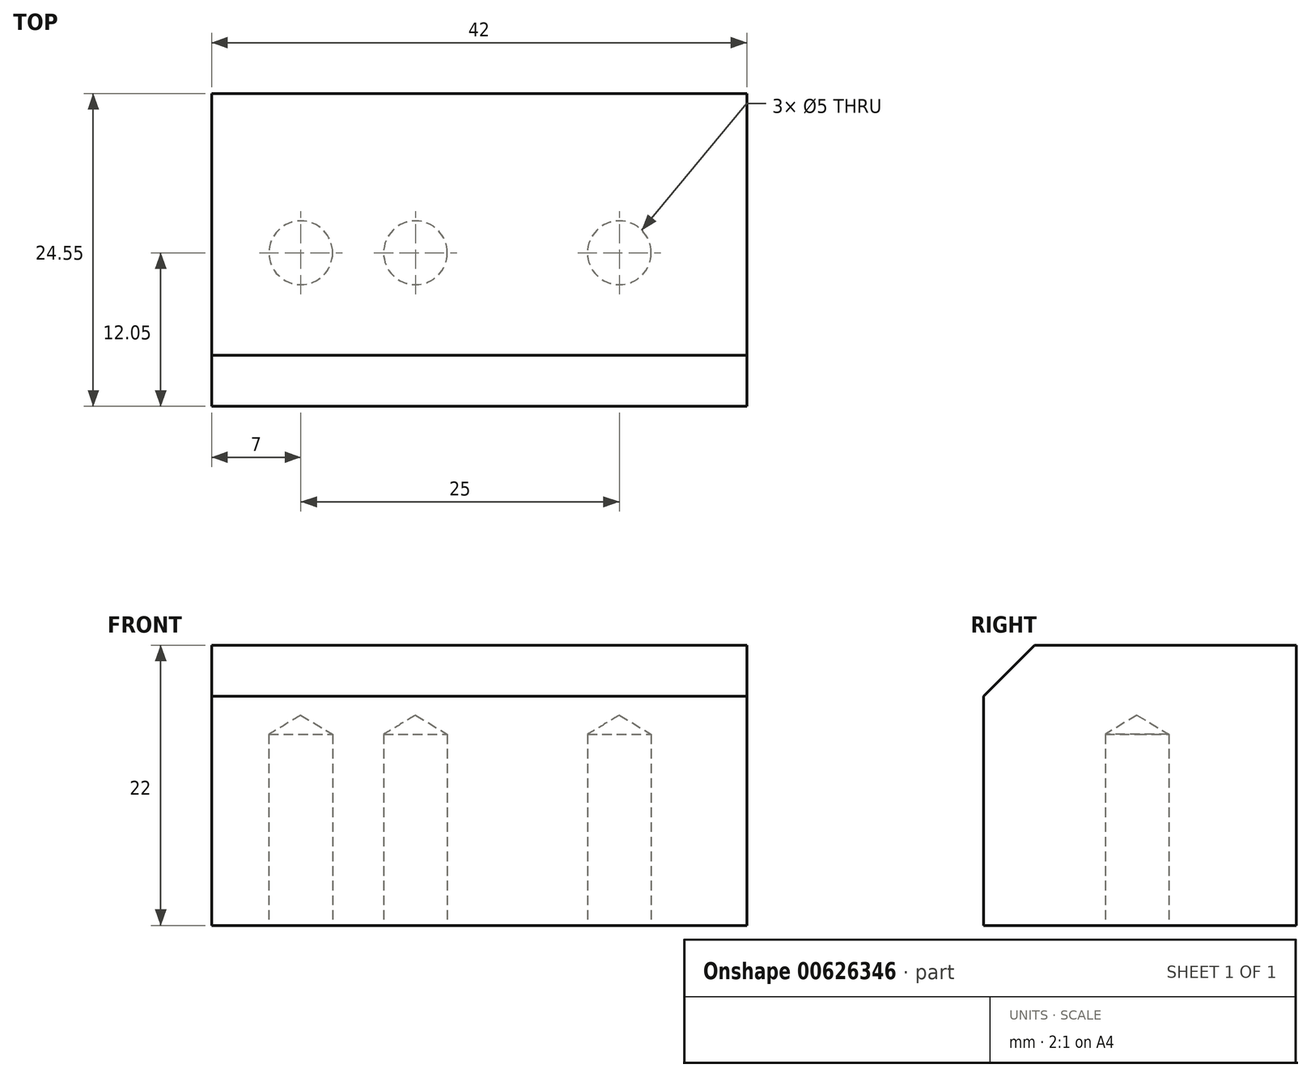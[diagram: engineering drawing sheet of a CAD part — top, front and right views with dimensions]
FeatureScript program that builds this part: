
annotation { "Feature Type Name" : "Feature", "Feature Type Description" : "" }
export const myFeature = defineFeature(function(context is Context, id is Id, definition is map)
    precondition{}
    {
        {
            var Q0;
            Q0=qCreatedBy(makeId("Right.planeOp"),FACE);
            var sketch = newSketch(context, id + "F0", { "sketchPlane" : qUnion([Q0])});
            skLineSegment(sketch, "E0.bottom", {"start": v(0, 0) * mm, "end": v(-24.55, 0) * mm});
            skLineSegment(sketch, "E0.top", {"start": v(0, 22) * mm, "end": v(-24.55, 22) * mm});
            skLineSegment(sketch, "E0.left", {"start": v(0, 0) * mm, "end": v(0, 22) * mm});
            skLineSegment(sketch, "E0.right", {"start": v(-24.55, 0) * mm, "end": v(-24.55, 22) * mm});
            skSolve(sketch);
        }
        {
            var Q0;
            Q0 = qSketchRegion(id + "F0", true);
            extrude(context, id + "F1", {"entities" : qUnion([Q0]), "depth" : 42 * mm, "offsetDistance" : 25 * mm});
        }
        {
            var Q0;
            Q0=makeQuery(id+"F1.opExtrude","SWEPT_EDGE",EDGE,{"disambiguationData":[OSD([sQuery(id+"F0.wireOp",EDGE,"E0.top"),sQuery(id+"F0.wireOp",EDGE,"E0.right")])]});
            chamfer(context, id + "F2", {"entities" : qUnion([Q0]), "width" : 4 * mm, "tangentPropagation" : true});
        }
        {
            var Q0;
            Q0=makeQuery(id+"F1.opExtrude","SWEPT_FACE",FACE,{"disambiguationData":[OSD([sQuery(id+"F0.wireOp",EDGE,"E0.bottom")])]});
            var sketch = newSketch(context, id + "F3", { "sketchPlane" : qUnion([Q0])});
            skPoint(sketch, "E1", {"position": v(32, 12.5) * mm});
            skPoint(sketch, "E2", {"position": v(16, 12.5) * mm});
            skPoint(sketch, "E3", {"position": v(7, 12.5) * mm});
            skSolve(sketch);
        }
        {
            var Q0;
            Q0=sQuery(id+"F3.wireOp",VERTEX,"E1");
            var Q1;
            Q1=sQuery(id+"F3.wireOp",VERTEX,"E2");
            var Q2;
            Q2=sQuery(id+"F3.wireOp",VERTEX,"E3");
            var Q3;
            Q3=makeQuery(id+"F1.opExtrude","SWEPT_BODY",BODY,{"disambiguationData":[OSD([sQuery(id+"F0.wireOp",EDGE,"E0.bottom"),sQuery(id+"F0.wireOp",EDGE,"E0.top"),sQuery(id+"F0.wireOp",EDGE,"E0.left"),sQuery(id+"F0.wireOp",EDGE,"E0.right")])]});
            hole(context, id + "F4", {"style" : HoleStyle.SIMPLE, "endStyle" : HoleEndStyle.BLIND, "standardTappedOrClearance" : lookupTablePath({ "standard" : "ISO", "engagement" : "75%", "pitch" : "1 mm", "size" : "M6", "type" : "Tapped" }), "standardBlindInLast" : lookupTablePath({ "standard" : "ISO", "engagement" : "75%", "pitch" : "1 mm", "size" : "M6", "type" : "Tapped" }), "holeDiameter" : 5 * mm, "majorDiameter" : 6 * mm, "showTappedDepth" : true, "holeDepth" : 15 * mm, "isTappedThrough" : true, "tappedDepth" : 12 * mm, "tapClearance" : 3, "locations" : qUnion([Q0, Q1, Q2]), "scope" : qUnion([Q3])});
        }
    });
